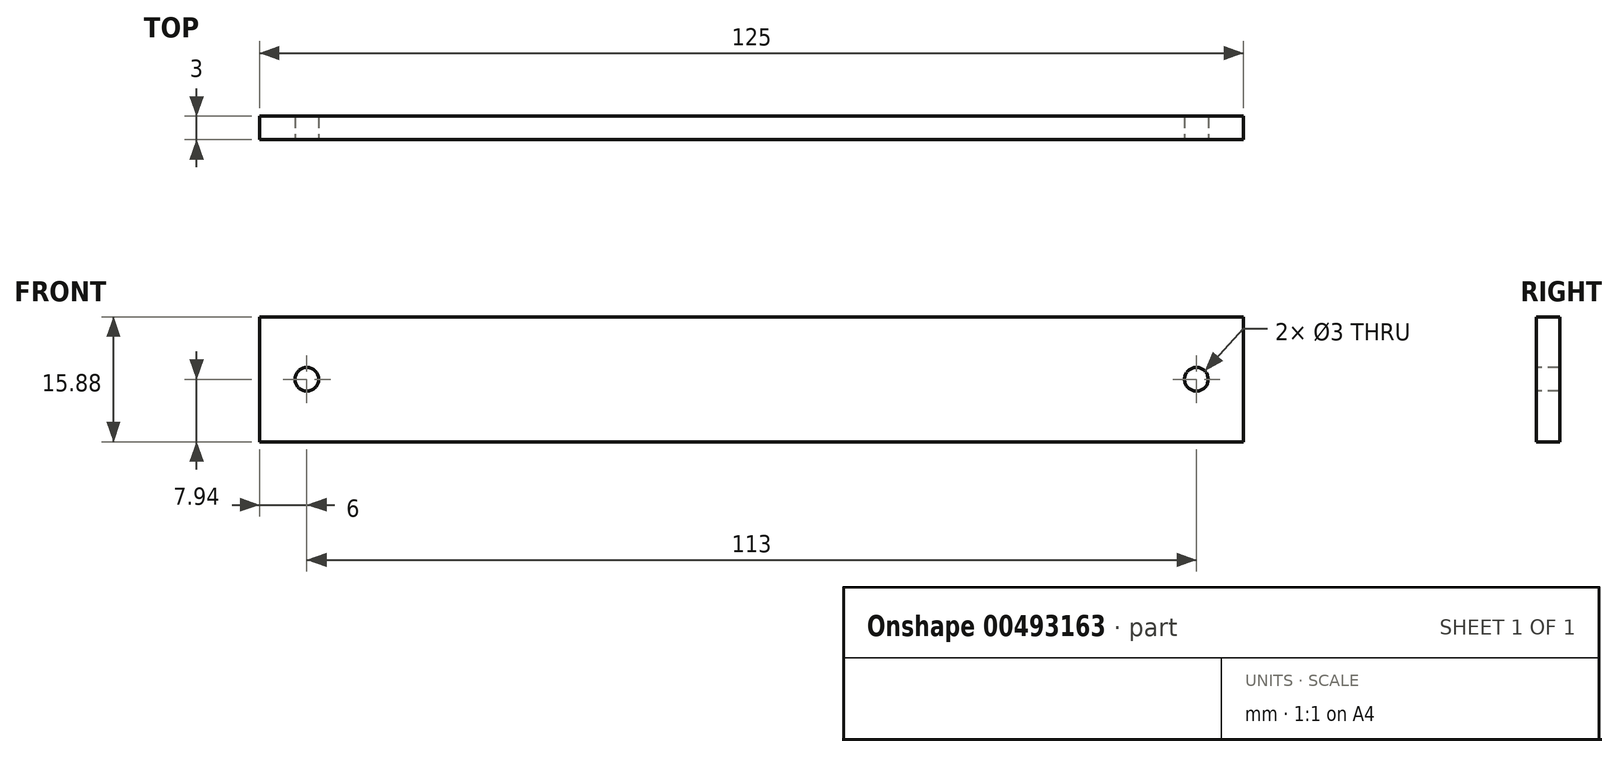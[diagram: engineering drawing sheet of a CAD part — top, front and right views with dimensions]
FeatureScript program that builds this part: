
annotation { "Feature Type Name" : "Feature", "Feature Type Description" : "" }
export const myFeature = defineFeature(function(context is Context, id is Id, definition is map)
    precondition{}
    {
        {
            var Q0;
            Q0=qCreatedBy(makeId("Front.planeOp"),FACE);
            var sketch = newSketch(context, id + "F0", { "sketchPlane" : qUnion([Q0])});
            skLineSegment(sketch, "E0.bottom", {"start": v(62.5, 7.94) * mm, "end": v(-62.5, 7.94) * mm});
            skLineSegment(sketch, "E0.top", {"start": v(62.5, -7.94) * mm, "end": v(-62.5, -7.94) * mm});
            skLineSegment(sketch, "E0.left", {"start": v(62.5, 7.94) * mm, "end": v(62.5, -7.94) * mm});
            skLineSegment(sketch, "E0.right", {"start": v(-62.5, 7.94) * mm, "end": v(-62.5, -7.94) * mm});
            skPoint(sketch, "E0.middle", {"position": v(0, 0) * mm});
            skSolve(sketch);
        }
        {
            var Q0;
            Q0 = qSketchRegion(id + "F0", true);
            extrude(context, id + "F1", {"entities" : qUnion([Q0]), "depth" : 3 * mm});
        }
        {
            var Q0;
            Q0=makeQuery(id+"F1.opExtrude","CAP_FACE",FACE,{"disambiguationData":[OSD([sQuery(id+"F0.wireOp",EDGE,"E0.bottom"),sQuery(id+"F0.wireOp",EDGE,"E0.top"),sQuery(id+"F0.wireOp",EDGE,"E0.left"),sQuery(id+"F0.wireOp",EDGE,"E0.right")])],"isStart":false});
            var sketch = newSketch(context, id + "F2", { "sketchPlane" : qUnion([Q0])});
            skLineSegment(sketch, "E1.bottom", {"start": v(-62.5, 7.94) * mm, "end": v(-50.5, 7.94) * mm, "construction": true});
            skLineSegment(sketch, "E1.top", {"start": v(-62.5, -7.94) * mm, "end": v(-50.5, -7.94) * mm, "construction": true});
            skLineSegment(sketch, "E1.left", {"start": v(-62.5, 7.94) * mm, "end": v(-62.5, -7.94) * mm, "construction": true});
            skLineSegment(sketch, "E1.right", {"start": v(-50.5, 7.94) * mm, "end": v(-50.5, -7.94) * mm, "construction": true});
            skLineSegment(sketch, "E2.bottom", {"start": v(62.5, 7.94) * mm, "end": v(50.5, 7.94) * mm, "construction": true});
            skLineSegment(sketch, "E2.top", {"start": v(62.5, -7.94) * mm, "end": v(50.5, -7.94) * mm, "construction": true});
            skLineSegment(sketch, "E2.left", {"start": v(62.5, 7.94) * mm, "end": v(62.5, -7.94) * mm, "construction": true});
            skLineSegment(sketch, "E2.right", {"start": v(50.5, 7.94) * mm, "end": v(50.5, -7.94) * mm, "construction": true});
            skLineSegment(sketch, "E3", {"start": v(-62.5, 7.94) * mm, "end": v(-50.5, -7.94) * mm, "construction": true});
            skLineSegment(sketch, "E4", {"start": v(50.5, -7.94) * mm, "end": v(62.5, 7.94) * mm, "construction": true});
            skCircle(sketch, "E5", {"center": v(-56.5, 0) * mm, "radius": 1.5 * mm});
            skCircle(sketch, "E6", {"center": v(56.5, 0) * mm, "radius": 1.5 * mm});
            skSolve(sketch);
        }
        {
            var Q0;
            Q0 = qSketchRegion(id + "F2", true);
            extrude(context, id + "F3", {"entities" : qUnion([Q0]), "operationType" : NewBodyOperationType.REMOVE, "oppositeDirection" : true, "depth" : 25 * mm});
        }
    });
